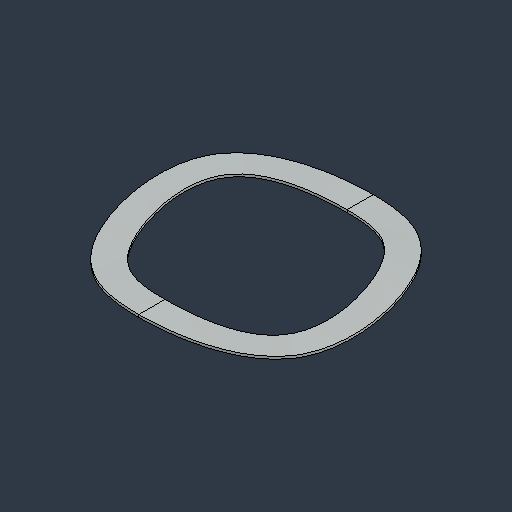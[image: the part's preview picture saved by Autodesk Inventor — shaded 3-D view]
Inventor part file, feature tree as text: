
AUTODESK INVENTOR PART (.ipt)
format: ipt  version: 2024.3 (Build 283343000, 343)  size: 117,248 bytes
history: native  units: in
note: dims shown in document units (in); Inventor stores cm internally (conversion verified against a paired STEP export)
features: loft x1
ambient origin geometry x8: Origin, YZ Plane, XZ Plane, XY Plane, X Axis, Y Axis, Z Axis, Center Point
bodies: Solid1 (feature_tree)
feature tree (1):
  loft  "Loft1"
